# Revit family: IS_ConnectAir_Multiproduct_BIM_DE;E0367;E0368
name_source: partatom
category: Plumbing Fixtures
revit_build: Autodesk Revit MEP 2014 (Build: 20130308_1515(x64)
units: mm (PartAtom-declared; Revit-internal decimal feet)

## types (2) — shared parameters
Accessories = www.idealstandard.de\ersatzteile
AreaUnits = millimeters
Assembly Code = C1030200
AssetType = Fixed
Brand = Ideal Standard
ConnectionType = Mechanical
DurationUnit = year
ExpectedLife = 25
Finish = white
GrossWeight = 0
IfcExportAs = IfcSanitaryTerminalType
IfcExportType = TOILETSEAT
InstallationInstructions = www.idealstandard.de\produkte
LinearUnits = millimeters
ManufacturerURL = www.idealstandard.com
NBSDescription = WC Seats and covers
NBSReference = 45-30-70/384
NettWeight = 2,2 kg
NominalHeight = 49 mm
NominalLength = 447 mm
NominalWidth = 367 mm
PanColor = White
PanMaterial = Duroplast
PanMounting = BackToWall
ProductInformation = www.idealstandard.de/produkte
Shape = Sculptured
Size = 365x445x50mm
Space = Internal
ToiletType = Other
URL = www.idealstandard.com
Uniclass2015Code = Pr_40_20_93_95
Uniclass2015Title = WC Seats and covers
Uniclass2015Version = Products v1.1
Version = 1
VolumeUnits = Litres
WarrantyDescription = Manufacturers Warranty
WarrantyDurationUnit = year
zero-valued in all types: CWFU, Cost, Default Elevation, HWFU, SpilloverLevel, WFU

## per-type parameters (varying)
| type | BIMObjectName | BarCode | Description | Features | Model | ModelNumber | ModelReference | Name |
| E036701 Connect Air toilet seat, wrap style, slow close | ISI_IdealStandard_WcSeatsAndCovers_ConnectAir_E036701 | 5017830514602 | E036701 Connect Air wrap style seat & cover, slow close | Connect Air wrap style seat & cover, slow close | E036701 | E036701 | Connect Air toilet seat, wrap style, slow close | WcSeatsAndCovers_ConnectAir_E036701_IdealStandard |
| E036801 Connect Air toilet seat, wrap style | ISI_IdealStandard_WcSeatsAndCovers_ConnectAir_E036801 | 5017830514619 | E036801 Connect Air wrap style seat & cover | Connect Air wrap style seat & cover | E036801 | E036801 | Connect Air toilet seat, wrap style | WcSeatsAndCovers_ConnectAir_E036801_IdealStandard |

## geometry (parser evidence)
native form markers: Sweep x1
no freeform markers — native parametric forms only
